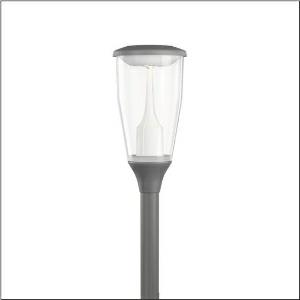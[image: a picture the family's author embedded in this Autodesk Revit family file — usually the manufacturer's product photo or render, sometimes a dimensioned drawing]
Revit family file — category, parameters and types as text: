
# Revit family: dl_11_iq___st1_2a_5xa5565kf14hp00022_5c81
name_source: partatom
category: Lighting Fixtures
units: mm (PartAtom-declared; Revit-internal decimal feet)

## family parameters
Cut with Voids When Loaded = No
Host = Face
Light Source = No
Part Type = Normal
Room Calculation Point = No
Round Connector Dimension = Use Diameter
Shared = No

## types (1)
- --- (1 x LED, 5060 lm, 33.6 W, 4000K)
    Apparent Load = 34 VA
    CIE Flux Codes = 23 60 93 95 100
    Color Rendering = 70
    Color Temperature = 4000K
    Default Elevation = 1800 mm
    Description = DL 11 iQ, mast luminaire, Module 540 iQ-SR, primary light control with 3 zone facetted reflector, of plastic, silver coated, highly specular, structured, primary optical cover: cover, of PMMA, transparent, light distribution: ST1.2a, light emission: direct distribution, primary light characteristic: asymmetric, installation type: post-top, LED, High Power LED, light colour: 740, colour temperature: 4000K, control gear: iQ Street-Remote, control: Street-Remote, Auto-Match, Temp-Guard, Lumen-Switch, Night-Set, Smart-Wire, Light-Fading, Desk-Remote (wireless, voltage-free reading and setting of iQ features in the workshop via application-optimized NFC function/RFID function), optimised constant luminous flux control (CLO 2.0), mains connection: 220..240V, AC, 50/60Hz, connection cable pre-assembled, cable length: 5,5m, start of lifetime: 34W, end of service life: 36W, luminaire housing, upper part, of diecast aluminium, coated, SITECO metallic grey (DB 702S), spigot size: 60mm (post-top), mounting height: 3..5m, post-top mast mounting element, of diecast aluminium, coated, SITECO metallic grey (DB 702S), Module 540 iQ-SR, traffic white (RAL 9016), equipment: Power, protection rating (complete): IP66, insulation class (complete): insulation class II (safety insulation), certification: CE, ENEC, ENEC+, VDE, impact resistance: IK07, packaging unit: 1 piece

Light Distribution: ST1.2a
    Height = 665 mm
    Lamp = 1 x LED
    Lamp Light Flux = 5060 lm
    Lamp Power = 33.6 W
    Lamp count = 1
    Length = 334 mm
    Luminous efficacy = 151 lm/W
    Manufacturer = Siteco
    ModVariant = No
    Model = 5XA5565KF14HP00022
    Number of Poles = 1
    OnlyDefault = Yes
    Power Factor = 1
    Product Name = DL 11 iQ | ST1.2a
    Product group = mast luminaire | pylon top
    ProductGroupID = 6100
    Protection Class = Protection class II
    Protection Degree = IP 66
    RLX_Detail_Level = 1
    RLX_Emergency_Light_Flux = 0 lm
    RLX_Emergency_Type = 0
    RLX_Emergency_Type_DB = No
    RlxData = <blob elided: 159789 chars, md5=82f25025>
    Socket = socket
    Standby Power = 0 W
    System Light Flux = 5060 lm
    System Power = 34 W
    Type Comments = factory setting: luminous flux: 100 % | dim-lin: 254 | 695 mA
    Type Image = l_1258354.jpg
    URL = http://relux.com
    VarID = @adj_040273
    Voltage = 0 V
    Weight = 0.00 kg
    Width = 0 mm  [stored 0 ft]

note: [stored X ft] marks values corroborated as IEEE doubles in the binary element streams (Revit-internal decimal feet)

## geometry (parser evidence)
native form markers: Blend x4, Sweep x10
no freeform markers — native parametric forms only
